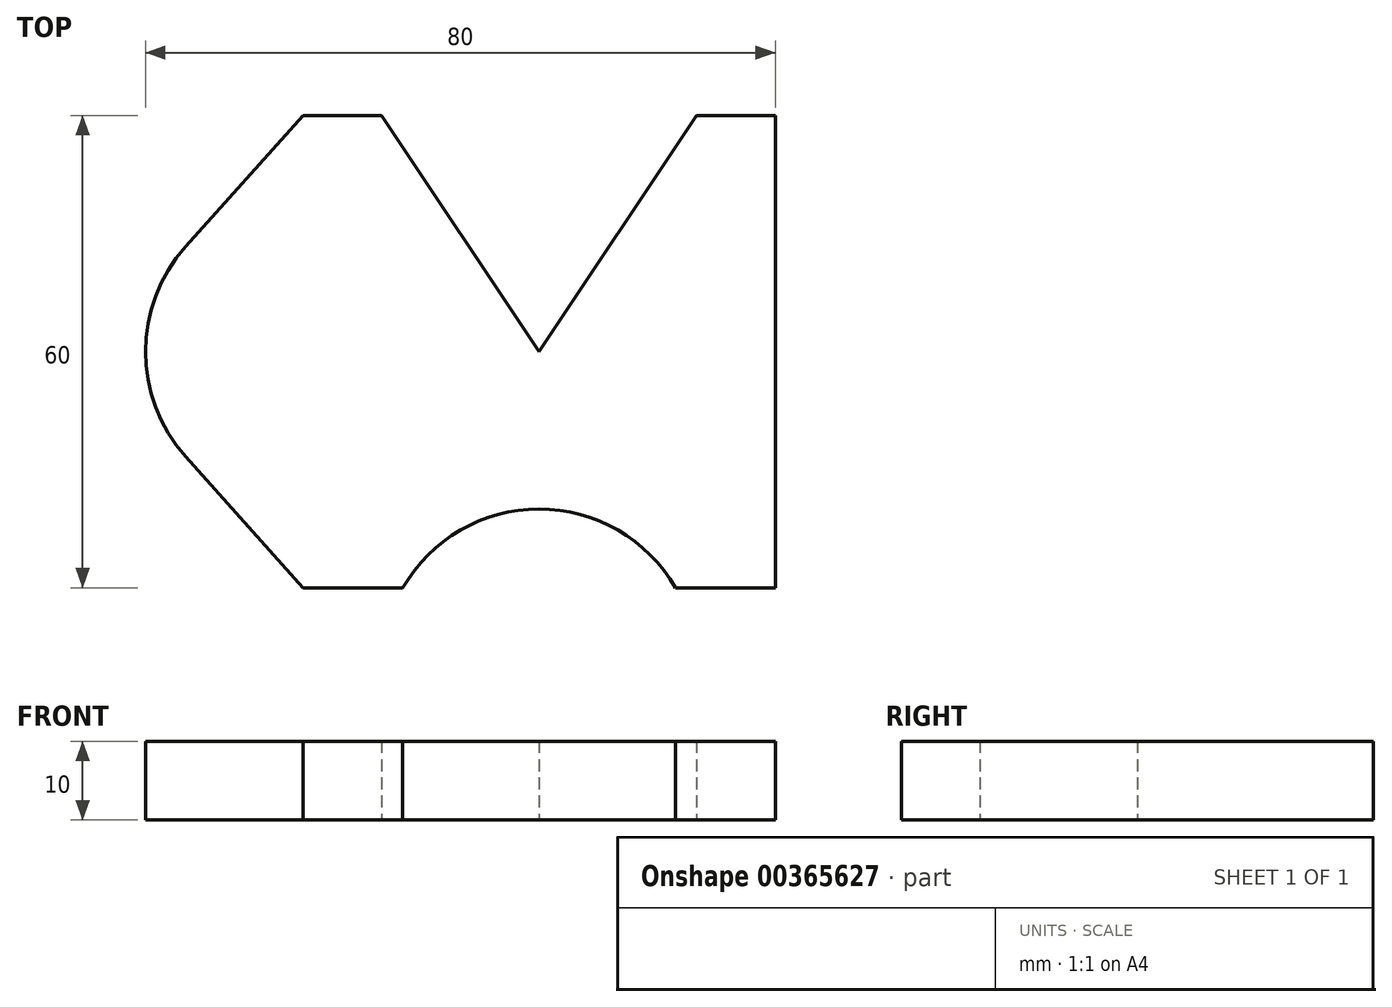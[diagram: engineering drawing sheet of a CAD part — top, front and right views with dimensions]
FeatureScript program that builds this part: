
annotation { "Feature Type Name" : "Feature", "Feature Type Description" : "" }
export const myFeature = defineFeature(function(context is Context, id is Id, definition is map)
    precondition{}
    {
        {
            var Q0;
            Q0=qCreatedBy(makeId("Top.planeOp"),FACE);
            var sketch = newSketch(context, id + "F0", { "sketchPlane" : qUnion([Q0])});
            skLineSegment(sketch, "E0", {"start": v(0, 0) * mm, "end": v(20, 30) * mm});
            skLineSegment(sketch, "E1", {"start": v(20, 30) * mm, "end": v(30, 30) * mm});
            skLineSegment(sketch, "E2", {"start": v(30, 30) * mm, "end": v(30, -30) * mm});
            skLineSegment(sketch, "E3", {"start": v(30, -30) * mm, "end": v(17.32, -30) * mm});
            skLineSegment(sketch, "E4", {"start": v(-20, 30) * mm, "end": v(0, 0) * mm});
            skLineSegment(sketch, "E5", {"start": v(-20, 30) * mm, "end": v(-30, 30) * mm});
            skLineSegment(sketch, "E6", {"start": v(-30, 30) * mm, "end": v(-44.9, 13.33) * mm});
            skArc(sketch, "E7", {"start": v(-44.9, 13.33) * mm, "mid": v(-50, 0) * mm, "end": v(-44.9, -13.33) * mm});
            skArc(sketch, "E8", {"start": v(17.32, -30) * mm, "mid": v(0, -20) * mm, "end": v(-17.32, -30) * mm});
            skLineSegment(sketch, "E9", {"start": v(-17.32, -30) * mm, "end": v(-30, -30) * mm});
            skLineSegment(sketch, "E10", {"start": v(-30, -30) * mm, "end": v(-44.9, -13.33) * mm});
            skLineSegment(sketch, "E11", {"start": v(-30, 70) * mm, "end": v(-30, -67.22) * mm, "construction": true});
            skSolve(sketch);
        }
        {
            var Q0;
            Q0=makeQuery(id+"F0.imprint","IMPRINT",FACE,{"disambiguationData":[TD([[makeQuery(id+"F0.imprint","IMPRINT",EDGE,{"derivedFrom":sQuery(id+"F0.wireOp",EDGE,"E0")}),-1.0]])]});
            extrude(context, id + "F1", {"entities" : qUnion([Q0]), "depth" : 10 * mm});
        }
    });
